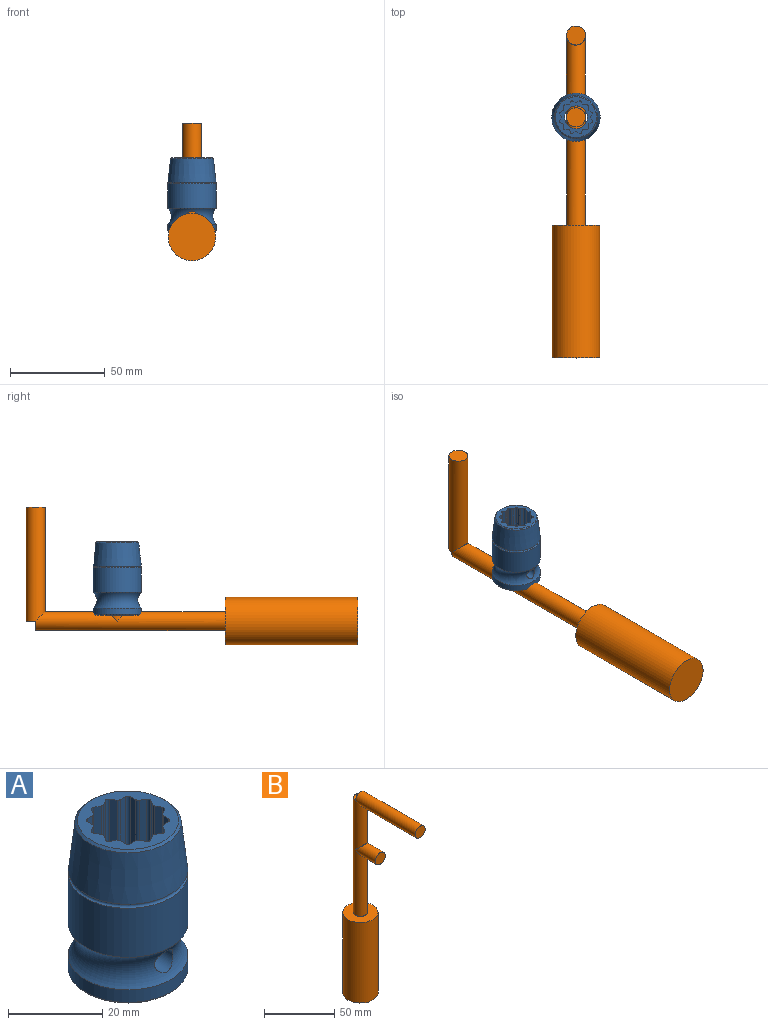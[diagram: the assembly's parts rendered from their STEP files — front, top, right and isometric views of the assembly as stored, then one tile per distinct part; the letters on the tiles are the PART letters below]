
ASSEMBLY  parts=2 mates=1
PART A: 66 faces, bbox 28.4x28.4x38.9 mm
  f0: plane 21.5x21.5mm, normal (0,0,1), area 149.7mm2, adj f1,f2,f3,f4,f5,f6,f7,f22
  f1: plane 16x1.64mm, normal (0,-1,0), area 26.3mm2, adj f0,f21,f39,f62
  f2: plane 16x1.64mm, normal (-1,0,0), area 26.3mm2, adj f0,f21,f41,f61
  f3: plane 16x1.42mm, normal (-0.87,0.5,0), area 26.3mm2, adj f0,f21,f40,f58
  f4: plane 16x1.42mm, normal (0.5,0.87,0), area 26.3mm2, adj f0,f21,f42,f57
  f5: plane 16x1.64mm, normal (1,0,0), area 26.3mm2, adj f0,f21,f45,f59
  f6: plane 16x1.64mm, normal (0,1,0), area 26.3mm2, adj f0,f21,f53,f61
  f7: plane 16x1.64mm, normal (-1,0,0), area 26.3mm2, adj f0,f21,f54,f62
  f8: cylinder r=6mm len=12mm, axis (0,0,1), area 223mm2, adj f20,f21
  f9: plane 24.5x24.5mm, normal (0,0,-1), area 307.6mm2, adj f15,f16,f17,f18,f19
  f10: cone r=12.69mm half-angle=6.4deg, axis (0,0,-1), area 942.5mm2, adj f14,f63
  f11: cylinder r=12.75mm len=25.5mm, axis (0,0,1), area 261.5mm2, adj f12,f15
  f12: torus R=17mm, axis (0,0,1), area 636mm2, adj f11,f13,f64,f65
  f13: cylinder r=12.75mm len=25.5mm, axis (0,0,1), area 1022.6mm2, adj f12,f14
  f14: torus R=12.75mm, axis (0,0,1), area 118.2mm2, adj f10,f13
  f15: cone r=12.75mm half-angle=45deg, axis (0,0,1), area 55.5mm2, adj f9,f11
  f16: plane 17x12.8mm, normal (0,1,0), area 193.8mm2, adj f9,f17,f19,f20,f65
  f17: plane 17x12.8mm, normal (1,0,0), area 217.6mm2, adj f9,f16,f18,f20
  f18: plane 17x12.8mm, normal (0,-1,0), area 193.8mm2, adj f9,f17,f19,f20,f64
  f19: plane 17x12.8mm, normal (-1,0,0), area 217.6mm2, adj f9,f16,f18,f20
  f20: plane 12.8x12.8mm, normal (0,0,-1), area 50.7mm2, adj f8,f16,f17,f18,f19
  f21: plane 17.25x17.25mm, normal (0,0,1), area 100.2mm2, adj f1,f2,f3,f4,f5,f6,f7,f8
  f22: plane 16x1.64mm, normal (0,-1,0), area 26.3mm2, adj f0,f21,f51,f59
  f23: plane 16x1.64mm, normal (1,0,0), area 26.3mm2, adj f0,f21,f52,f60
  f24: plane 16x1.64mm, normal (0,1,0), area 26.3mm2, adj f0,f21,f43,f60
  f25: plane 16x1.42mm, normal (-0.5,-0.87,0), area 26.3mm2, adj f0,f21,f54,f58
  f26: plane 16x1.42mm, normal (-0.87,0.5,0), area 26.3mm2, adj f0,f21,f53,f57
  f27: plane 16x1.42mm, normal (0.5,0.87,0), area 26.3mm2, adj f0,f21,f52,f56
  f28: plane 16x1.42mm, normal (0.87,-0.5,0), area 26.3mm2, adj f0,f21,f44,f56
  f29: plane 16x1.42mm, normal (-0.5,-0.87,0), area 26.3mm2, adj f0,f21,f46,f55
  f30: plane 16x1.42mm, normal (0.87,-0.5,0), area 26.3mm2, adj f0,f21,f51,f55
  f31: plane 16x1.42mm, normal (0.5,-0.87,0), area 26.3mm2, adj f0,f21,f46,f47
  f32: plane 16x1.42mm, normal (-0.87,-0.5,0), area 26.3mm2, adj f0,f21,f39,f47
  f33: plane 16x1.42mm, normal (0.87,0.5,0), area 26.3mm2, adj f0,f21,f44,f48
  f34: plane 16x1.42mm, normal (0.5,-0.87,0), area 26.3mm2, adj f0,f21,f45,f48
  f35: plane 16x1.42mm, normal (-0.5,0.87,0), area 26.3mm2, adj f0,f21,f42,f49
  f36: plane 16x1.42mm, normal (0.87,0.5,0), area 26.3mm2, adj f0,f21,f43,f49
  f37: plane 16x1.42mm, normal (-0.87,-0.5,0), area 26.3mm2, adj f0,f21,f40,f50
  f38: plane 16x1.42mm, normal (-0.5,0.87,0), area 26.3mm2, adj f0,f21,f41,f50
  f39: cylinder r=0.7mm len=16mm, axis (0,0,-1), area 11.7mm2, adj f0,f1,f21,f32
  f40: cylinder r=0.7mm len=16mm, axis (0,0,1), area 11.7mm2, adj f0,f3,f21,f37
  f41: cylinder r=0.7mm len=16mm, axis (0,0,-1), area 11.7mm2, adj f0,f2,f21,f38
  f42: cylinder r=0.7mm len=16mm, axis (0,0,1), area 11.7mm2, adj f0,f4,f21,f35
  f43: cylinder r=0.7mm len=16mm, axis (0,0,-1), area 11.7mm2, adj f0,f21,f24,f36
  f44: cylinder r=0.7mm len=16mm, axis (0,0,1), area 11.7mm2, adj f0,f21,f28,f33
  f45: cylinder r=0.7mm len=16mm, axis (0,0,-1), area 11.7mm2, adj f0,f5,f21,f34
  f46: cylinder r=0.7mm len=16mm, axis (0,0,1), area 11.7mm2, adj f0,f21,f29,f31
  f47: cylinder r=0.7mm len=16mm, axis (0,0,1), area 17.6mm2, adj f0,f21,f31,f32
  f48: cylinder r=0.7mm len=16mm, axis (0,0,-1), area 17.6mm2, adj f0,f21,f33,f34
  f49: cylinder r=0.7mm len=16mm, axis (0,0,1), area 17.6mm2, adj f0,f21,f35,f36
  f50: cylinder r=0.7mm len=16mm, axis (0,0,-1), area 17.6mm2, adj f0,f21,f37,f38
  f51: cylinder r=0.7mm len=16mm, axis (0,0,1), area 11.7mm2, adj f0,f21,f22,f30
  f52: cylinder r=0.7mm len=16mm, axis (0,0,1), area 11.7mm2, adj f0,f21,f23,f27
  f53: cylinder r=0.7mm len=16mm, axis (0,0,1), area 11.7mm2, adj f0,f6,f21,f26
  f54: cylinder r=0.7mm len=16mm, axis (0,0,1), area 11.7mm2, adj f0,f7,f21,f25
  f55: cylinder r=0.7mm len=16mm, axis (0,0,1), area 17.6mm2, adj f0,f21,f29,f30
  f56: cylinder r=0.7mm len=16mm, axis (0,0,-1), area 17.6mm2, adj f0,f21,f27,f28
  f57: cylinder r=0.7mm len=16mm, axis (0,0,1), area 17.6mm2, adj f0,f4,f21,f26
  f58: cylinder r=0.7mm len=16mm, axis (0,0,-1), area 17.6mm2, adj f0,f3,f21,f25
  f59: cylinder r=0.7mm len=16mm, axis (0,0,1), area 17.6mm2, adj f0,f5,f21,f22
  f60: cylinder r=0.7mm len=16mm, axis (0,0,-1), area 17.6mm2, adj f0,f21,f23,f24
  f61: cylinder r=0.7mm len=16mm, axis (0,0,1), area 17.6mm2, adj f0,f2,f6,f21
  f62: cylinder r=0.7mm len=16mm, axis (0,0,-1), area 17.6mm2, adj f0,f1,f7,f21
  f63: cone r=10.75mm half-angle=48.2deg, axis (0,0,-1), area 51.6mm2, adj f0,f10
  f64: cylinder r=2.75mm len=5.5mm, axis (0,-1,0), area 82.2mm2, adj f12,f18
  f65: cylinder r=2.75mm len=5.5mm, axis (0,-1,0), area 82.2mm2, adj f12,f16
PART B: 10 faces, bbox 25x72.5x175 mm
  f0: cylinder r=5mm len=100mm, axis (0,0,-1), area 2991.6mm2, adj f1,f2,f4,f9
  f1: plane 10x5mm, normal (0,0,1), area 39.3mm2, adj f0,f6
  f2: cylinder r=5mm len=20mm, axis (0,1,0), area 528.3mm2, adj f0,f3
  f3: plane 10x10mm, normal (0,-1,0), area 78.5mm2, adj f2
  f4: cylinder r=5mm len=60mm, axis (0,1,0), area 1835mm2, adj f0,f5,f6
  f5: plane 10x10mm, normal (0,-1,0), area 78.5mm2, adj f4
  f6: plane 10x5mm, normal (0,1,0), area 39.3mm2, adj f1,f4
  f7: cylinder r=12.5mm len=70mm, axis (0,0,1), area 5497.8mm2, adj f8,f9
  f8: plane 25x25mm, normal (0,0,-1), area 490.9mm2, adj f7
  f9: plane 25x25mm, normal (0,0,1), area 412.3mm2, adj f0,f7
PLACE A t=(0,0,-52.5)mm
PLACE B rot(axis=(-1,0,0),90deg) t=(0,-56.91,-55.5)mm
MATE slider B.f2 <-> A.f8  axis (0,0,1) through (0,0,-35.5)mm
